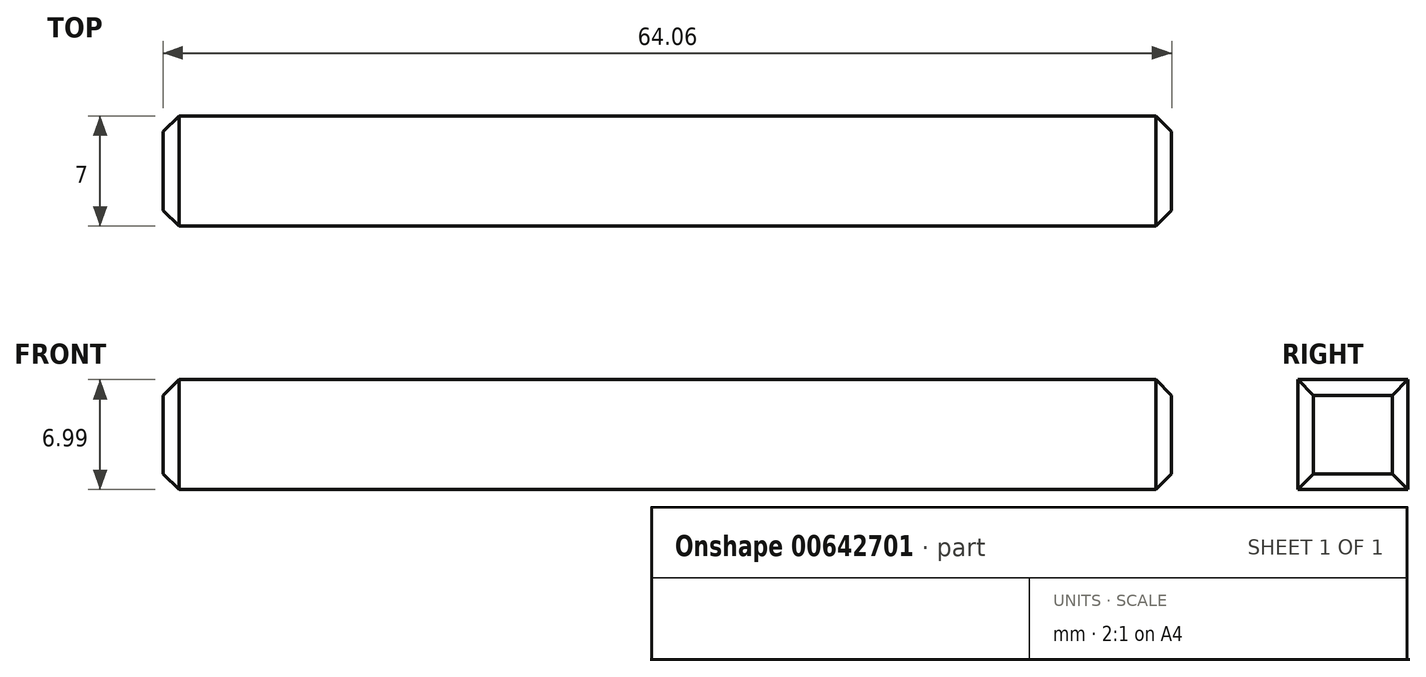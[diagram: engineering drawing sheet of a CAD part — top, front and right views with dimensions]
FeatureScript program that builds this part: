
annotation { "Feature Type Name" : "Feature", "Feature Type Description" : "" }
export const myFeature = defineFeature(function(context is Context, id is Id, definition is map)
    precondition{}
    {
        {
            var Q0;
            Q0=qCreatedBy(makeId("Front.planeOp"),FACE);
            var sketch = newSketch(context, id + "F0", { "sketchPlane" : qUnion([Q0])});
            skLineSegment(sketch, "E0", {"start": v(-33.3, 0) * mm, "end": v(-33.3, 6.99) * mm});
            skLineSegment(sketch, "E1", {"start": v(-33.3, 6.99) * mm, "end": v(30.76, 6.99) * mm});
            skLineSegment(sketch, "E2", {"start": v(30.76, 6.99) * mm, "end": v(30.76, 0) * mm});
            skLineSegment(sketch, "E3", {"start": v(30.76, 0) * mm, "end": v(-33.3, 0) * mm});
            skSolve(sketch);
        }
        {
            var Q0;
            Q0=makeQuery(id+"F0.imprint","IMPRINT",FACE,{"disambiguationData":[TD([[makeQuery(id+"F0.imprint","IMPRINT",EDGE,{"derivedFrom":sQuery(id+"F0.wireOp",EDGE,"E0")}),-1.0]])]});
            extrude(context, id + "F1", {"entities" : qUnion([Q0]), "depth" : 7 * mm, "offsetDistance" : 25 * mm});
        }
        {
            var Q0;
            Q0=makeQuery(id+"F1.opExtrude","SWEPT_EDGE",EDGE,{"disambiguationData":[OSD([sQuery(id+"F0.wireOp",EDGE,"E1"),sQuery(id+"F0.wireOp",EDGE,"E2")])]});
            var Q1;
            Q1=makeQuery(id+"F1.opExtrude","CAP_EDGE",EDGE,{"disambiguationData":[OSD([sQuery(id+"F0.wireOp",EDGE,"E2")])],"isStart":false});
            var Q2;
            Q2=makeQuery(id+"F1.opExtrude","SWEPT_EDGE",EDGE,{"disambiguationData":[OSD([sQuery(id+"F0.wireOp",EDGE,"E2"),sQuery(id+"F0.wireOp",EDGE,"E3")])]});
            var Q3;
            Q3=makeQuery(id+"F1.opExtrude","CAP_EDGE",EDGE,{"disambiguationData":[OSD([sQuery(id+"F0.wireOp",EDGE,"E2")])],"isStart":true});
            chamfer(context, id + "F2", {"entities" : qUnion([Q0, Q1, Q2, Q3]), "width" : 1 * mm, "tangentPropagation" : true});
        }
        {
            var Q0;
            Q0=makeQuery(id+"F1.opExtrude","SWEPT_EDGE",EDGE,{"disambiguationData":[OSD([sQuery(id+"F0.wireOp",EDGE,"E0"),sQuery(id+"F0.wireOp",EDGE,"E1")])]});
            var Q1;
            Q1=makeQuery(id+"F1.opExtrude","CAP_EDGE",EDGE,{"disambiguationData":[OSD([sQuery(id+"F0.wireOp",EDGE,"E0")])],"isStart":true});
            var Q2;
            Q2=makeQuery(id+"F1.opExtrude","SWEPT_EDGE",EDGE,{"disambiguationData":[OSD([sQuery(id+"F0.wireOp",EDGE,"E0"),sQuery(id+"F0.wireOp",EDGE,"E3")])]});
            var Q3;
            Q3=makeQuery(id+"F1.opExtrude","CAP_EDGE",EDGE,{"disambiguationData":[OSD([sQuery(id+"F0.wireOp",EDGE,"E0")])],"isStart":false});
            chamfer(context, id + "F3", {"entities" : qUnion([Q0, Q1, Q2, Q3]), "width" : 1 * mm, "tangentPropagation" : true});
        }
    });
